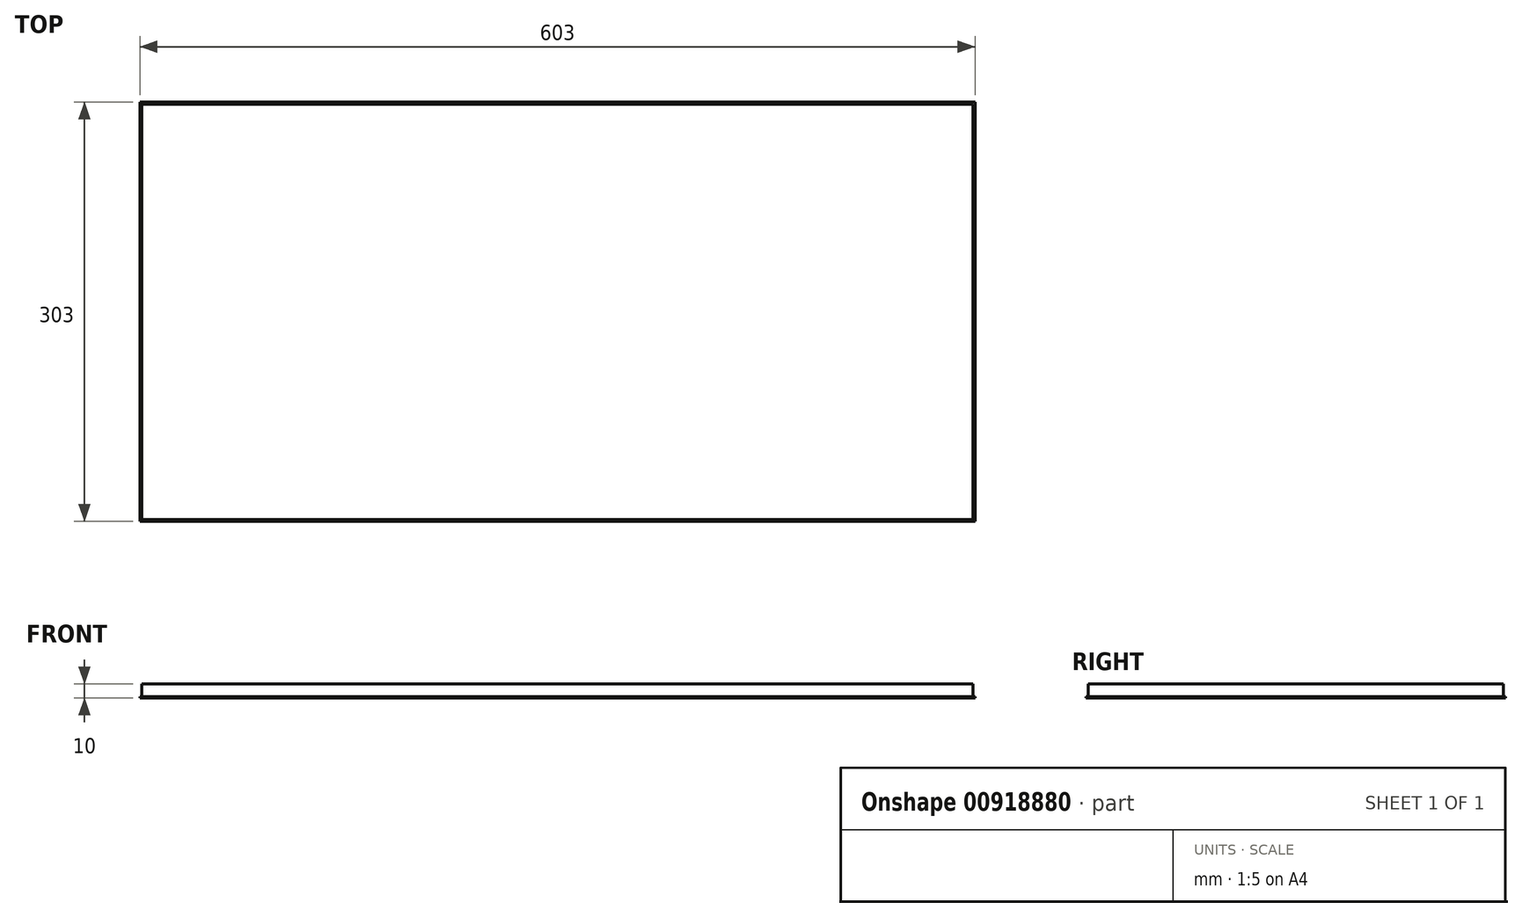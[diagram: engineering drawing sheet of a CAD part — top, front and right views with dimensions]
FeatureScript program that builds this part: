
annotation { "Feature Type Name" : "Feature", "Feature Type Description" : "" }
export const myFeature = defineFeature(function(context is Context, id is Id, definition is map)
    precondition{}
    {
        {
            var Q0;
            Q0=qCreatedBy(makeId("Top.planeOp"),FACE);
            var sketch = newSketch(context, id + "F0", { "sketchPlane" : qUnion([Q0])});
            skLineSegment(sketch, "E0.bottom", {"start": v(-1564.43, 2175.09) * mm, "end": v(-964.43, 2175.09) * mm});
            skLineSegment(sketch, "E0.top", {"start": v(-1564.43, 1875.09) * mm, "end": v(-964.43, 1875.09) * mm});
            skLineSegment(sketch, "E0.left", {"start": v(-1564.43, 2175.09) * mm, "end": v(-1564.43, 1875.09) * mm});
            skLineSegment(sketch, "E0.right", {"start": v(-964.43, 2175.09) * mm, "end": v(-964.43, 1875.09) * mm});
            skLineSegment(sketch, "E1.0", {"start": v(-1565.93, 2176.59) * mm, "end": v(-962.93, 2176.59) * mm});
            skLineSegment(sketch, "E1.1", {"start": v(-1565.93, 2176.59) * mm, "end": v(-1565.93, 1873.59) * mm});
            skLineSegment(sketch, "E1.2", {"start": v(-1565.93, 1873.59) * mm, "end": v(-962.93, 1873.59) * mm});
            skLineSegment(sketch, "E1.3", {"start": v(-962.93, 2176.59) * mm, "end": v(-962.93, 1873.59) * mm});
            skSolve(sketch);
        }
        {
            var Q0;
            Q0=makeQuery(id+"F0.imprint","IMPRINT",FACE,{"disambiguationData":[TD([[makeQuery(id+"F0.imprint","IMPRINT",EDGE,{"derivedFrom":sQuery(id+"F0.wireOp",EDGE,"E0.bottom")}),-1.0]])]});
            extrude(context, id + "F1", {"entities" : qUnion([Q0]), "depth" : 10 * mm, "offsetDistance" : 25 * mm});
        }
        {
            var Q0;
            Q0 = qSketchRegion(id + "F0", true);
            extrude(context, id + "F2", {"entities" : qUnion([Q0]), "operationType" : NewBodyOperationType.ADD, "depth" : 1 * mm, "offsetDistance" : 25 * mm});
        }
    });
